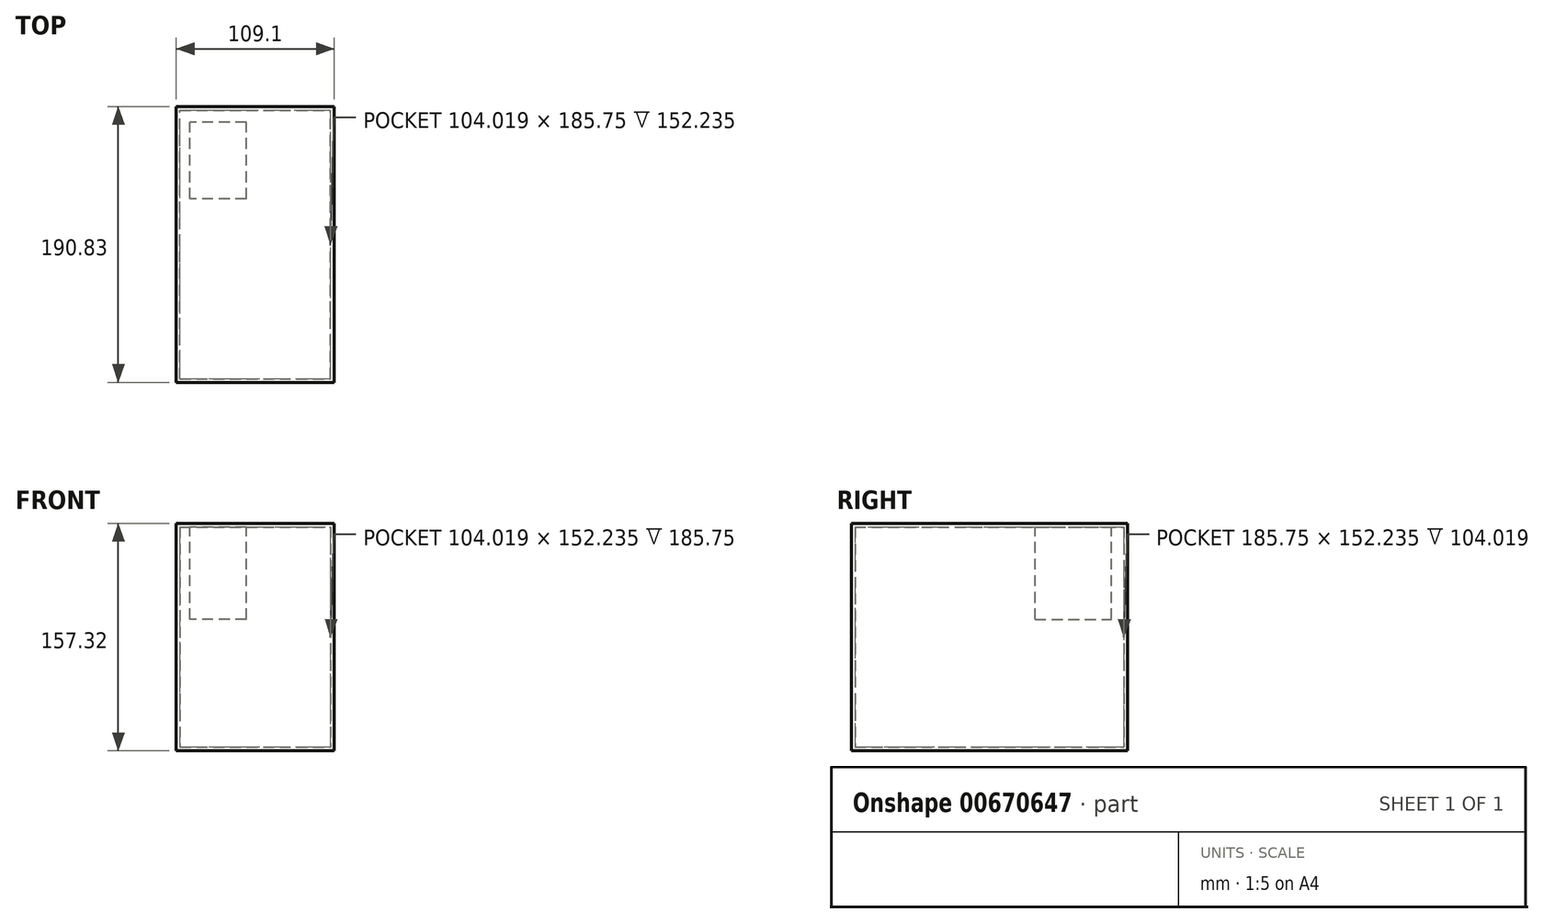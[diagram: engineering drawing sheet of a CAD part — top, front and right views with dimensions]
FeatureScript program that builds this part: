
annotation { "Feature Type Name" : "Feature", "Feature Type Description" : "" }
export const myFeature = defineFeature(function(context is Context, id is Id, definition is map)
    precondition{}
    {
        {
            var Q0;
            Q0=qCreatedBy(makeId("Front.planeOp"),FACE);
            var sketch = newSketch(context, id + "F0", { "sketchPlane" : qUnion([Q0])});
            skLineSegment(sketch, "E0.bottom", {"start": v(-34.57, 31.2) * mm, "end": v(21.2, 31.2) * mm});
            skLineSegment(sketch, "E0.top", {"start": v(-34.57, -16.5) * mm, "end": v(21.2, -16.5) * mm});
            skLineSegment(sketch, "E0.left", {"start": v(-34.57, 31.2) * mm, "end": v(-34.57, -16.5) * mm});
            skLineSegment(sketch, "E0.right", {"start": v(21.2, 31.2) * mm, "end": v(21.2, -16.5) * mm});
            skSolve(sketch);
        }
        {
            var Q0;
            Q0=makeQuery(id+"F0.imprint","IMPRINT",FACE,{"disambiguationData":[TD([[makeQuery(id+"F0.imprint","IMPRINT",EDGE,{"derivedFrom":sQuery(id+"F0.wireOp",EDGE,"E0.bottom")}),-1.0]])]});
            var Q1;
            Q1 = qSketchRegion(id + "F0", true);
            extrude(context, id + "F1", {"entities" : qUnion([Q0, Q1]), "depth" : 25.4 * mm, "offsetDistance" : 25.4 * mm});
        }
        {
            var Q0;
            Q0=makeQuery(id+"F1.opExtrude","CAP_FACE",FACE,{"disambiguationData":[OSD([sQuery(id+"F0.wireOp",EDGE,"E0.bottom"),sQuery(id+"F0.wireOp",EDGE,"E0.top"),sQuery(id+"F0.wireOp",EDGE,"E0.left"),sQuery(id+"F0.wireOp",EDGE,"E0.right")])],"isStart":false});
            extrude(context, id + "F2", {"entities" : qUnion([Q0]), "operationType" : NewBodyOperationType.ADD, "depth" : 101.6 * mm, "offsetDistance" : 25.4 * mm});
        }
        {
            var Q0;
            {var subQ0=sQuery(id+"F0.wireOp",EDGE,"E0.left");Q0=makeQuery(id+"F2.boolean.opBoolean","MERGE",FACE,{"derivedFrom":[makeQuery(id+"F1.opExtrude","SWEPT_FACE",FACE,{"disambiguationData":[OSD([subQ0])]}),makeQuery(id+"F2.opExtrude","SWEPT_FACE",FACE,{"disambiguationData":[OSD([subQ0])]})]});}
            extrude(context, id + "F3", {"entities" : qUnion([Q0]), "operationType" : NewBodyOperationType.ADD, "depth" : 105.94 * mm, "offsetDistance" : 25.4 * mm});
        }
        {
            var Q0;
            {var subQ0=sQuery(id+"F0.wireOp",EDGE,"E0.bottom");Q0=makeQuery(id+"F3.boolean.opBoolean","MERGE",FACE,{"derivedFrom":[makeQuery(id+"F2.boolean.opBoolean","MERGE",FACE,{"derivedFrom":[makeQuery(id+"F1.opExtrude","SWEPT_FACE",FACE,{"disambiguationData":[OSD([subQ0])]}),makeQuery(id+"F2.opExtrude","SWEPT_FACE",FACE,{"disambiguationData":[OSD([subQ0])]})]}),makeQuery(id+"F3.opExtrude","SWEPT_FACE",FACE,{"disambiguationData":[OSD([subQ0,sQuery(id+"F0.wireOp",EDGE,"E0.left")])]})]});}
            var sketch = newSketch(context, id + "F4", { "sketchPlane" : qUnion([Q0])});
            skSolve(sketch);
        }
        {
            var Q0;
            {var subQ1=sQuery(id+"F0.wireOp",EDGE,"E0.bottom");var subQ2=sQuery(id+"F0.wireOp",EDGE,"E0.left");Q0=makeQuery(id+"F4.imprint","IMPRINT",FACE,{"disambiguationData":[TD([[makeQuery(id+"F4.imprint","IMPRINT",EDGE,{"derivedFrom":makeQuery(id+"F3.opExtrude","CAP_EDGE",EDGE,{"disambiguationData":[OSD([subQ1,subQ2])],"isStart":false})}),-1.0]])]});}
            extrude(context, id + "F5", {"entities" : qUnion([Q0]), "operationType" : NewBodyOperationType.ADD, "depth" : 109.62 * mm, "offsetDistance" : 25.4 * mm});
        }
        {
            var Q0;
            {var subQ0=sQuery(id+"F0.wireOp",EDGE,"E0.top");Q0=makeQuery(id+"F3.boolean.opBoolean","MERGE",FACE,{"derivedFrom":[makeQuery(id+"F2.boolean.opBoolean","MERGE",FACE,{"derivedFrom":[makeQuery(id+"F1.opExtrude","SWEPT_FACE",FACE,{"disambiguationData":[OSD([subQ0])]}),makeQuery(id+"F2.opExtrude","SWEPT_FACE",FACE,{"disambiguationData":[OSD([subQ0])]})]}),makeQuery(id+"F3.opExtrude","SWEPT_FACE",FACE,{"disambiguationData":[OSD([subQ0,sQuery(id+"F0.wireOp",EDGE,"E0.left")])]})]});}
            extrude(context, id + "F6", {"entities" : qUnion([Q0]), "operationType" : NewBodyOperationType.ADD, "oppositeDirection" : true, "depth" : 21.23 * mm, "offsetDistance" : 25.4 * mm});
        }
        {
            var Q0;
            {var subQ0=sQuery(id+"F0.wireOp",EDGE,"E0.left");var subQ1=sQuery(id+"F0.wireOp",EDGE,"E0.bottom");Q0=makeQuery(id+"F5.boolean.opBoolean","MERGE",FACE,{"derivedFrom":[makeQuery(id+"F3.opExtrude","CAP_FACE",FACE,{"disambiguationData":[OSD([subQ0])],"isStart":false}),makeQuery(id+"F5.opExtrude","SWEPT_FACE",FACE,{"disambiguationData":[OSD([subQ1,subQ0]),TDD([makeQuery(id+"F4.imprint","IMPRINT",EDGE,{"derivedFrom":makeQuery(id+"F3.opExtrude","CAP_EDGE",EDGE,{"disambiguationData":[OSD([subQ1,subQ0])],"isStart":false})})])]})]});}
            extrude(context, id + "F7", {"entities" : qUnion([Q0]), "operationType" : NewBodyOperationType.REMOVE, "oppositeDirection" : true, "depth" : 52.62 * mm, "offsetDistance" : 25.4 * mm});
        }
        {
            var Q0;
            {var subQ0=sQuery(id+"F0.wireOp",EDGE,"E0.left");var subQ1=sQuery(id+"F0.wireOp",EDGE,"E0.bottom");Q0=makeQuery(id+"F5.boolean.opBoolean","MERGE",FACE,{"derivedFrom":[makeQuery(id+"F3.boolean.opBoolean","MERGE",FACE,{"derivedFrom":[makeQuery(id+"F1.opExtrude","CAP_FACE",FACE,{"disambiguationData":[OSD([subQ1,sQuery(id+"F0.wireOp",EDGE,"E0.top"),subQ0,sQuery(id+"F0.wireOp",EDGE,"E0.right")])],"isStart":true}),makeQuery(id+"F3.opExtrude","SWEPT_FACE",FACE,{"disambiguationData":[OSD([subQ0]),TDD([makeQuery(id+"F1.opExtrude","CAP_EDGE",EDGE,{"disambiguationData":[OSD([subQ0])],"isStart":true})])]})]}),makeQuery(id+"F5.opExtrude","SWEPT_FACE",FACE,{"disambiguationData":[OSD([subQ1,subQ0]),TDD([makeQuery(id+"F4.imprint","IMPRINT",EDGE,{"derivedFrom":makeQuery(id+"F3.boolean.opBoolean","MERGE",EDGE,{"derivedFrom":[makeQuery(id+"F1.opExtrude","CAP_EDGE",EDGE,{"disambiguationData":[OSD([subQ1])],"isStart":true}),makeQuery(id+"F3.opExtrude","SWEPT_EDGE",EDGE,{"disambiguationData":[OSD([subQ1,subQ0]),TDD([makeQuery(id+"F1.opExtrude","CAP_VERTEX",VERTEX,{"disambiguationData":[OSD([subQ1,subQ0])],"isStart":true})])]})]})})])]})]});}
            extrude(context, id + "F8", {"entities" : qUnion([Q0]), "operationType" : NewBodyOperationType.ADD, "depth" : 63.83 * mm, "offsetDistance" : 25.4 * mm});
        }
        {
            var Q0;
            {var subQ0=sQuery(id+"F0.wireOp",EDGE,"E0.left");var subQ1=sQuery(id+"F0.wireOp",EDGE,"E0.bottom");Q0=makeQuery(id+"F8.boolean.opBoolean","MERGE",FACE,{"derivedFrom":[makeQuery(id+"F7.boolean.opBoolean","COPY",FACE,{"derivedFrom":makeQuery(id+"F7.opExtrude","CAP_FACE",FACE,{"disambiguationData":[OSD([subQ1,subQ0])],"isStart":false})}),makeQuery(id+"F8.opExtrude","SWEPT_FACE",FACE,{"disambiguationData":[OSD([subQ1,subQ0]),TDD([makeQuery(id+"F7.boolean.opBoolean","COPY",EDGE,{"derivedFrom":makeQuery(id+"F7.opExtrude","CAP_EDGE",EDGE,{"disambiguationData":[OSD([subQ1,subQ0]),TDD([makeQuery(id+"F5.boolean.opBoolean","MERGE",EDGE,{"derivedFrom":[makeQuery(id+"F3.opExtrude","CAP_EDGE",EDGE,{"disambiguationData":[OSD([subQ0]),TDD([makeQuery(id+"F1.opExtrude","CAP_EDGE",EDGE,{"disambiguationData":[OSD([subQ0])],"isStart":true})])],"isStart":false}),makeQuery(id+"F5.opExtrude","SWEPT_EDGE",EDGE,{"disambiguationData":[OSD([subQ1,subQ0]),TDD([makeQuery(id+"F4.imprint","INTERSECT",VERTEX,{"derivedFrom":[makeQuery(id+"F3.opExtrude","CAP_EDGE",EDGE,{"disambiguationData":[OSD([subQ1,subQ0])],"isStart":false}),makeQuery(id+"F3.boolean.opBoolean","MERGE",EDGE,{"derivedFrom":[makeQuery(id+"F1.opExtrude","CAP_EDGE",EDGE,{"disambiguationData":[OSD([subQ1])],"isStart":true}),makeQuery(id+"F3.opExtrude","SWEPT_EDGE",EDGE,{"disambiguationData":[OSD([subQ1,subQ0]),TDD([makeQuery(id+"F1.opExtrude","CAP_VERTEX",VERTEX,{"disambiguationData":[OSD([subQ1,subQ0])],"isStart":true})])]})]})]})])]})]})])],"isStart":false})})])]})]});}
            var sketch = newSketch(context, id + "F9", { "sketchPlane" : qUnion([Q0])});
            skLineSegment(sketch, "E1.bottom", {"start": v(4.7, 67.67) * mm, "end": v(70.63, 67.67) * mm});
            skLineSegment(sketch, "E1.top", {"start": v(4.7, 0) * mm, "end": v(70.63, 0) * mm});
            skLineSegment(sketch, "E1.left", {"start": v(4.7, 67.67) * mm, "end": v(4.7, 0) * mm});
            skLineSegment(sketch, "E1.right", {"start": v(70.63, 67.67) * mm, "end": v(70.63, 0) * mm});
            skSolve(sketch);
        }
        {
            var Q0;
            Q0=makeQuery(id+"F9.imprint","IMPRINT",FACE,{"disambiguationData":[TD([[makeQuery(id+"F9.imprint","IMPRINT",EDGE,{"derivedFrom":sQuery(id+"F9.wireOp",EDGE,"E1.bottom")}),-1.0]])]});
            extrude(context, id + "F10", {"entities" : qUnion([Q0]), "operationType" : NewBodyOperationType.ADD, "oppositeDirection" : true, "depth" : 22.51 * mm, "offsetDistance" : 25.4 * mm});
        }
        {
            var Q0;
            {var subQ0=sQuery(id+"F0.wireOp",EDGE,"E0.left");var subQ1=sQuery(id+"F0.wireOp",EDGE,"E0.bottom");Q0=makeQuery(id+"F8.boolean.opBoolean","MERGE",FACE,{"derivedFrom":[makeQuery(id+"F5.opExtrude","CAP_FACE",FACE,{"disambiguationData":[OSD([subQ1,subQ0,sQuery(id+"F0.wireOp",EDGE,"E0.right")])],"isStart":false}),makeQuery(id+"F8.opExtrude","SWEPT_FACE",FACE,{"disambiguationData":[OSD([subQ1,subQ0]),TDD([makeQuery(id+"F5.opExtrude","CAP_EDGE",EDGE,{"disambiguationData":[OSD([subQ1,subQ0]),TDD([makeQuery(id+"F4.imprint","IMPRINT",EDGE,{"derivedFrom":makeQuery(id+"F3.boolean.opBoolean","MERGE",EDGE,{"derivedFrom":[makeQuery(id+"F1.opExtrude","CAP_EDGE",EDGE,{"disambiguationData":[OSD([subQ1])],"isStart":true}),makeQuery(id+"F3.opExtrude","SWEPT_EDGE",EDGE,{"disambiguationData":[OSD([subQ1,subQ0]),TDD([makeQuery(id+"F1.opExtrude","CAP_VERTEX",VERTEX,{"disambiguationData":[OSD([subQ1,subQ0])],"isStart":true})])]})]})})])],"isStart":false})])]})]});}
            var Q1;
            Q1=makeQuery(id+"F1.opExtrude","SWEPT_BODY",BODY,{"disambiguationData":[OSD([sQuery(id+"F0.wireOp",EDGE,"E0.bottom"),sQuery(id+"F0.wireOp",EDGE,"E0.top"),sQuery(id+"F0.wireOp",EDGE,"E0.left"),sQuery(id+"F0.wireOp",EDGE,"E0.right")])]});
            shell(context, id + "F11", {"isHollow" : true, "entities" : qUnion([Q0]), "parts" : qUnion([Q1]), "thickness" : 2.54 * mm});
        }
        {
            var Q0;
            {var subQ0=sQuery(id+"F0.wireOp",EDGE,"E0.left");var subQ1=sQuery(id+"F0.wireOp",EDGE,"E0.bottom");Q0=makeQuery(id+"F8.boolean.opBoolean","MERGE",FACE,{"derivedFrom":[makeQuery(id+"F5.opExtrude","CAP_FACE",FACE,{"disambiguationData":[OSD([subQ1,subQ0,sQuery(id+"F0.wireOp",EDGE,"E0.right")])],"isStart":false}),makeQuery(id+"F8.opExtrude","SWEPT_FACE",FACE,{"disambiguationData":[OSD([subQ1,subQ0]),TDD([makeQuery(id+"F5.opExtrude","CAP_EDGE",EDGE,{"disambiguationData":[OSD([subQ1,subQ0]),TDD([makeQuery(id+"F4.imprint","IMPRINT",EDGE,{"derivedFrom":makeQuery(id+"F3.boolean.opBoolean","MERGE",EDGE,{"derivedFrom":[makeQuery(id+"F1.opExtrude","CAP_EDGE",EDGE,{"disambiguationData":[OSD([subQ1])],"isStart":true}),makeQuery(id+"F3.opExtrude","SWEPT_EDGE",EDGE,{"disambiguationData":[OSD([subQ1,subQ0]),TDD([makeQuery(id+"F1.opExtrude","CAP_VERTEX",VERTEX,{"disambiguationData":[OSD([subQ1,subQ0])],"isStart":true})])]})]})})])],"isStart":false})])]})]});}
            var sketch = newSketch(context, id + "F12", { "sketchPlane" : qUnion([Q0])});
            skLineSegment(sketch, "E2.bottom", {"start": v(-39.51, 0) * mm, "end": v(-78.56, 0) * mm});
            skLineSegment(sketch, "E2.top", {"start": v(-39.51, 52.83) * mm, "end": v(-78.56, 52.83) * mm});
            skLineSegment(sketch, "E2.left", {"start": v(-39.51, 0) * mm, "end": v(-39.51, 52.83) * mm});
            skLineSegment(sketch, "E2.right", {"start": v(-78.56, 0) * mm, "end": v(-78.56, 52.83) * mm});
            skSolve(sketch);
        }
        {
            var Q0;
            Q0=makeQuery(id+"F12.imprint","IMPRINT",FACE,{"disambiguationData":[TD([[makeQuery(id+"F12.imprint","IMPRINT",EDGE,{"derivedFrom":sQuery(id+"F12.wireOp",EDGE,"E2.bottom")}),-1.0]])]});
            extrude(context, id + "F13", {"entities" : qUnion([Q0]), "operationType" : NewBodyOperationType.ADD, "oppositeDirection" : true, "depth" : 66.33 * mm, "offsetDistance" : 25.4 * mm});
        }
    });
